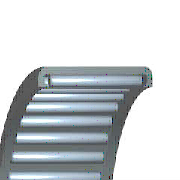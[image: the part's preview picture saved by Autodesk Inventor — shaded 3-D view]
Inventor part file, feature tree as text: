
AUTODESK INVENTOR PART (.ipt)
format: ipt  version: 2020 (Build 240168000, 168)  size: 293,376 bytes
history: native  units: mm (DEFAULTED — no unit token found)
features: sketch x1, other x1, pattern_circular x1
ambient origin geometry x8: Origin, YZ Plane, XZ Plane, XY Plane, X Axis, Y Axis, Z Axis, Center Point
bodies: Solid1 (feature_tree), Body (feature_tree)
feature tree (3):
  sketch  "Sketch"  dims[d36=90.0deg d0=1.25mm d1=0.25mm d39=90.0deg d2=170.0mm d3=360.0deg d4=0.0mm d5=0.0mm d6=1.4mm d7=0.0mm d8=10.0mm d9=14.0mm d10=11.0mm d11=12.0mm d12=1.0mm d13=1.9mm d14=7.0mm d57=0.0mm d58=0.0mm]
  other  "Roller"
  pattern_circular  "Rollers"  [2 undecoded]
note: 2 required parameter values undecoded (feature->parameter linkage not recoverable at this tier; creation-order binding heuristic only, values carry confidence <= 0.55)
